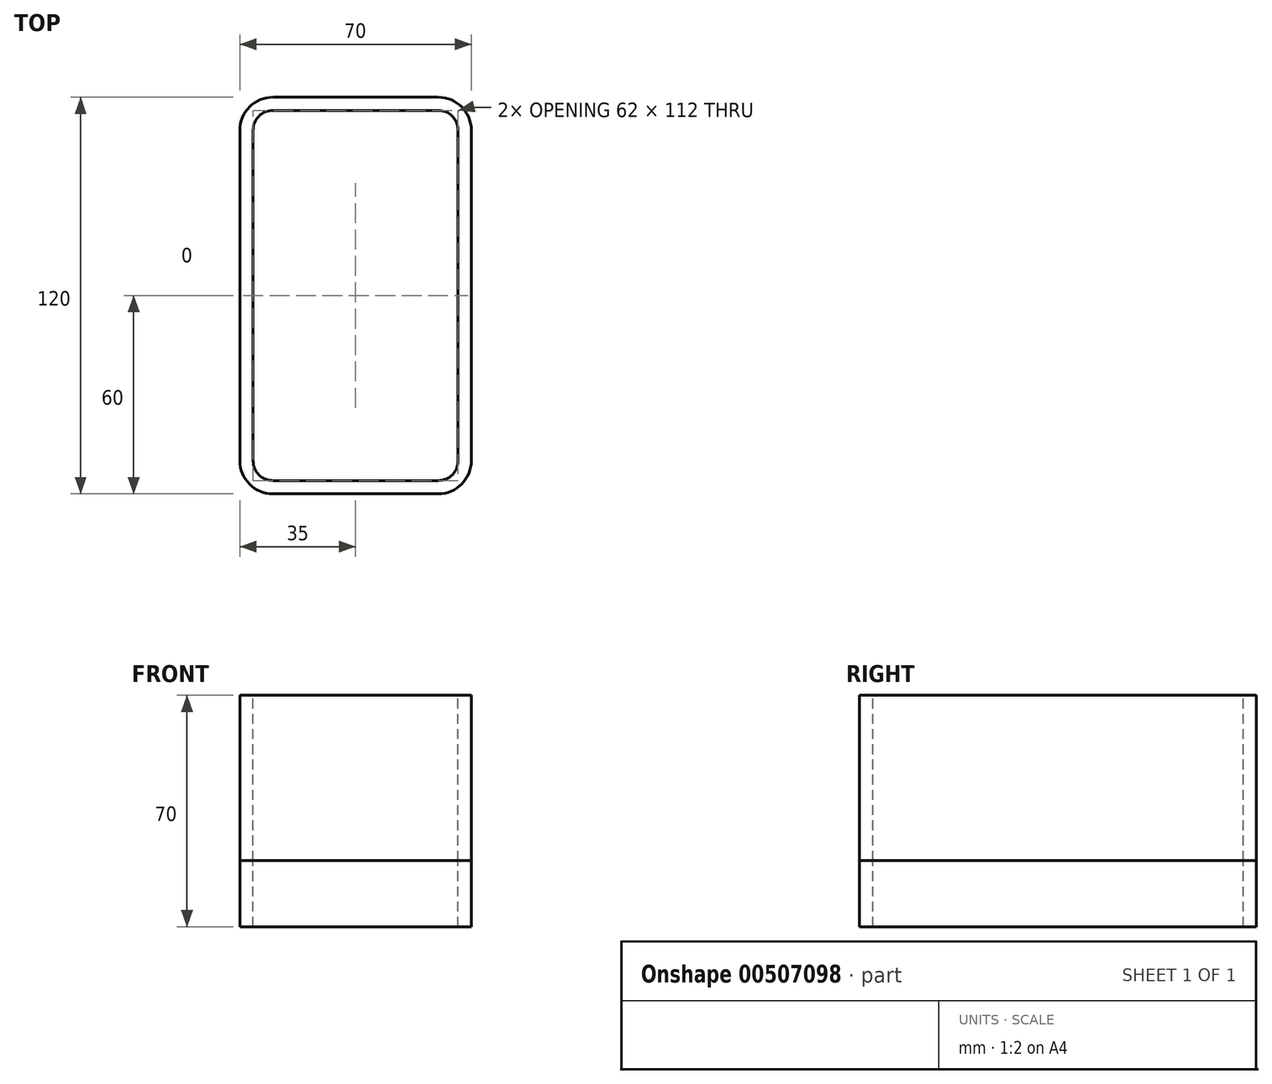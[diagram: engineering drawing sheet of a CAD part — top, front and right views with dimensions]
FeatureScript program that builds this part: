
annotation { "Feature Type Name" : "Feature", "Feature Type Description" : "" }
export const myFeature = defineFeature(function(context is Context, id is Id, definition is map)
    precondition{}
    {
        {
            var Q0;
            Q0=qCreatedBy(makeId("Top.planeOp"),FACE);
            var sketch = newSketch(context, id + "F0", { "sketchPlane" : qUnion([Q0])});
            skCircle(sketch, "E0", {"center": v(-7.28, 0) * mm, "radius": 2.5 * mm});
            skCircle(sketch, "E1", {"center": v(5.45, 0) * mm, "radius": 4 * mm});
            skSolve(sketch);
        }
        {
            var Q0;
            Q0 = qSketchRegion(id + "F0", true);
            extrude(context, id + "F1", {"entities" : qUnion([Q0]), "depth" : 35 * mm, "offsetDistance" : 25 * mm});
        }
        {
            var Q0;
            Q0=makeQuery(id+"F1.opExtrude","CAP_EDGE",EDGE,{"disambiguationData":[OSD([sQuery(id+"F0.wireOp",EDGE,"E1")])],"isStart":false});
            chamfer(context, id + "F2", {"entities" : qUnion([Q0]), "chamferType" : ChamferType.OFFSET_ANGLE, "width" : 3 * mm, "oppositeDirection" : false, "angle" : 70 * degree, "tangentPropagation" : true});
        }
        {
            var Q0;
            Q0=makeQuery(id+"F1.opExtrude","CAP_EDGE",EDGE,{"disambiguationData":[OSD([sQuery(id+"F0.wireOp",EDGE,"E0")])],"isStart":false});
            chamfer(context, id + "F3", {"entities" : qUnion([Q0]), "chamferType" : ChamferType.OFFSET_ANGLE, "width" : 1.5 * mm, "oppositeDirection" : false, "angle" : 80 * degree, "tangentPropagation" : true});
        }
        {
            var Q0;
            Q0=qCreatedBy(makeId("Top.planeOp"),FACE);
            var sketch = newSketch(context, id + "F4", { "sketchPlane" : qUnion([Q0])});
            skLineSegment(sketch, "E2.bottom", {"start": v(35, 60) * mm, "end": v(-35, 60) * mm});
            skLineSegment(sketch, "E2.top", {"start": v(35, -60) * mm, "end": v(-35, -60) * mm});
            skLineSegment(sketch, "E2.left", {"start": v(35, 60) * mm, "end": v(35, -60) * mm});
            skLineSegment(sketch, "E2.right", {"start": v(-35, 60) * mm, "end": v(-35, -60) * mm});
            skPoint(sketch, "E2.middle", {"position": v(0, 0) * mm});
            skSolve(sketch);
        }
        {
            var Q0;
            Q0 = qSketchRegion(id + "F4", true);
            extrude(context, id + "F5", {"entities" : qUnion([Q0]), "depth" : 50 * mm, "offsetDistance" : 25 * mm});
        }
        {
            var Q0;
            Q0=makeQuery(id+"F5.opExtrude","SWEPT_EDGE",EDGE,{"disambiguationData":[OSD([sQuery(id+"F4.wireOp",EDGE,"E2.bottom"),sQuery(id+"F4.wireOp",EDGE,"E2.right")])]});
            var Q1;
            Q1=makeQuery(id+"F5.opExtrude","SWEPT_EDGE",EDGE,{"disambiguationData":[OSD([sQuery(id+"F4.wireOp",EDGE,"E2.bottom"),sQuery(id+"F4.wireOp",EDGE,"E2.left")])]});
            var Q2;
            Q2=makeQuery(id+"F5.opExtrude","SWEPT_EDGE",EDGE,{"disambiguationData":[OSD([sQuery(id+"F4.wireOp",EDGE,"E2.top"),sQuery(id+"F4.wireOp",EDGE,"E2.left")])]});
            var Q3;
            Q3=makeQuery(id+"F5.opExtrude","SWEPT_EDGE",EDGE,{"disambiguationData":[OSD([sQuery(id+"F4.wireOp",EDGE,"E2.top"),sQuery(id+"F4.wireOp",EDGE,"E2.right")])]});
            fillet(context, id + "F6", {"entities" : qUnion([Q0, Q1, Q2, Q3]), "radius" : 10 * mm, "tangentPropagation" : true, "allowEdgeOverflow" : false});
        }
        {
            var Q0;
            Q0=makeQuery(id+"F5.opExtrude","CAP_FACE",FACE,{"disambiguationData":[OSD([sQuery(id+"F4.wireOp",EDGE,"E2.bottom"),sQuery(id+"F4.wireOp",EDGE,"E2.top"),sQuery(id+"F4.wireOp",EDGE,"E2.left"),sQuery(id+"F4.wireOp",EDGE,"E2.right")])],"isStart":true});
            extrude(context, id + "F7", {"entities" : qUnion([Q0]), "depth" : 20 * mm, "offsetDistance" : 25 * mm});
        }
        {
            var Q0;
            Q0=qCreatedBy(makeId("Top.planeOp"),FACE);
            var sketch = newSketch(context, id + "F8", { "sketchPlane" : qUnion([Q0])});
            skArc(sketch, "E3.0", {"start": v(-31, -50) * mm, "mid": v(-29.24, -54.24) * mm, "end": v(-25, -56) * mm});
            skLineSegment(sketch, "E3.1", {"start": v(-31, 50) * mm, "end": v(-31, -50) * mm});
            skLineSegment(sketch, "E3.2", {"start": v(-25, -56) * mm, "end": v(25, -56) * mm});
            skArc(sketch, "E3.3", {"start": v(-25, 56) * mm, "mid": v(-29.24, 54.24) * mm, "end": v(-31, 50) * mm});
            skArc(sketch, "E3.4", {"start": v(25, -56) * mm, "mid": v(29.24, -54.24) * mm, "end": v(31, -50) * mm});
            skLineSegment(sketch, "E3.5", {"start": v(31, -50) * mm, "end": v(31, 50) * mm});
            skArc(sketch, "E3.6", {"start": v(31, 50) * mm, "mid": v(29.24, 54.24) * mm, "end": v(25, 56) * mm});
            skLineSegment(sketch, "E3.7", {"start": v(25, 56) * mm, "end": v(-25, 56) * mm});
            skSolve(sketch);
        }
        {
            var Q0;
            Q0 = qSketchRegion(id + "F8", true);
            extrude(context, id + "F9", {"entities" : qUnion([Q0]), "operationType" : NewBodyOperationType.REMOVE, "endBound" : BoundingType.THROUGH_ALL, "oppositeDirection" : true, "depth" : 25 * mm, "offsetDistance" : 25 * mm, "hasSecondDirection" : true, "secondDirectionBound" : SecondDirectionBoundingType.THROUGH_ALL, "secondDirectionOppositeDirection" : false, "secondDirectionDepth" : 25 * mm});
        }
    });
